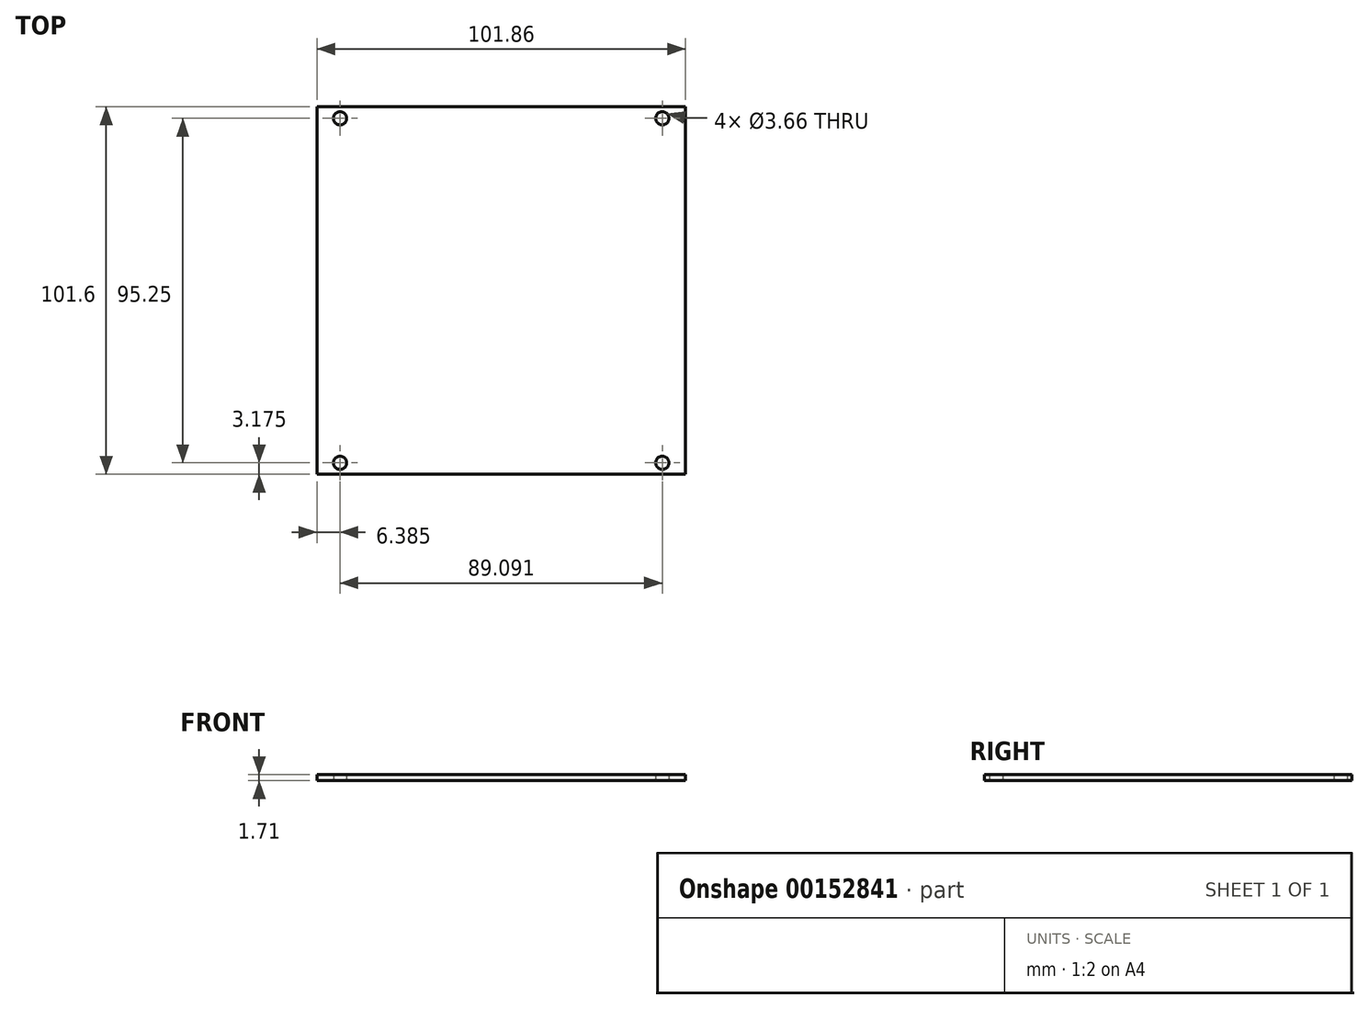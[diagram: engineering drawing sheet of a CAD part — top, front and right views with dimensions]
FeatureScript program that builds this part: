
annotation { "Feature Type Name" : "Feature", "Feature Type Description" : "" }
export const myFeature = defineFeature(function(context is Context, id is Id, definition is map)
    precondition{}
    {
        {
            var Q0;
            Q0=qCreatedBy(makeId("Top.planeOp"),FACE);
            var sketch = newSketch(context, id + "F0", { "sketchPlane" : qUnion([Q0])});
            skLineSegment(sketch, "E0.bottom", {"start": v(50.93, 50.8) * mm, "end": v(-50.93, 50.8) * mm});
            skLineSegment(sketch, "E0.top", {"start": v(50.93, -50.8) * mm, "end": v(-50.93, -50.8) * mm});
            skLineSegment(sketch, "E0.left", {"start": v(50.93, 50.8) * mm, "end": v(50.93, -50.8) * mm});
            skLineSegment(sketch, "E0.right", {"start": v(-50.93, 50.8) * mm, "end": v(-50.93, -50.8) * mm});
            skPoint(sketch, "E0.middle", {"position": v(0, 0) * mm});
            skLineSegment(sketch, "E1.bottom", {"start": v(44.55, 47.62) * mm, "end": v(-44.55, 47.62) * mm, "construction": true});
            skLineSegment(sketch, "E1.top", {"start": v(44.55, -47.62) * mm, "end": v(-44.55, -47.62) * mm, "construction": true});
            skLineSegment(sketch, "E1.left", {"start": v(44.55, 47.62) * mm, "end": v(44.55, -47.62) * mm, "construction": true});
            skLineSegment(sketch, "E1.right", {"start": v(-44.55, 47.62) * mm, "end": v(-44.55, -47.62) * mm, "construction": true});
            skLineSegment(sketch, "E2", {"start": v(44.55, 47.62) * mm, "end": v(44.55, 50.8) * mm, "construction": true});
            skLineSegment(sketch, "E3", {"start": v(44.55, 47.62) * mm, "end": v(50.93, 47.62) * mm, "construction": true});
            skCircle(sketch, "E4", {"center": v(-44.55, 47.62) * mm, "radius": 1.83 * mm});
            skCircle(sketch, "E5", {"center": v(44.55, 47.62) * mm, "radius": 1.83 * mm});
            skCircle(sketch, "E6", {"center": v(44.55, -47.62) * mm, "radius": 1.83 * mm});
            skCircle(sketch, "E7", {"center": v(-44.55, -47.62) * mm, "radius": 1.83 * mm});
            skSolve(sketch);
        }
        {
            var Q0;
            Q0 = qSketchRegion(id + "F0", true);
            extrude(context, id + "F1", {"entities" : qUnion([Q0]), "depth" : 1.7 * mm});
        }
    });
